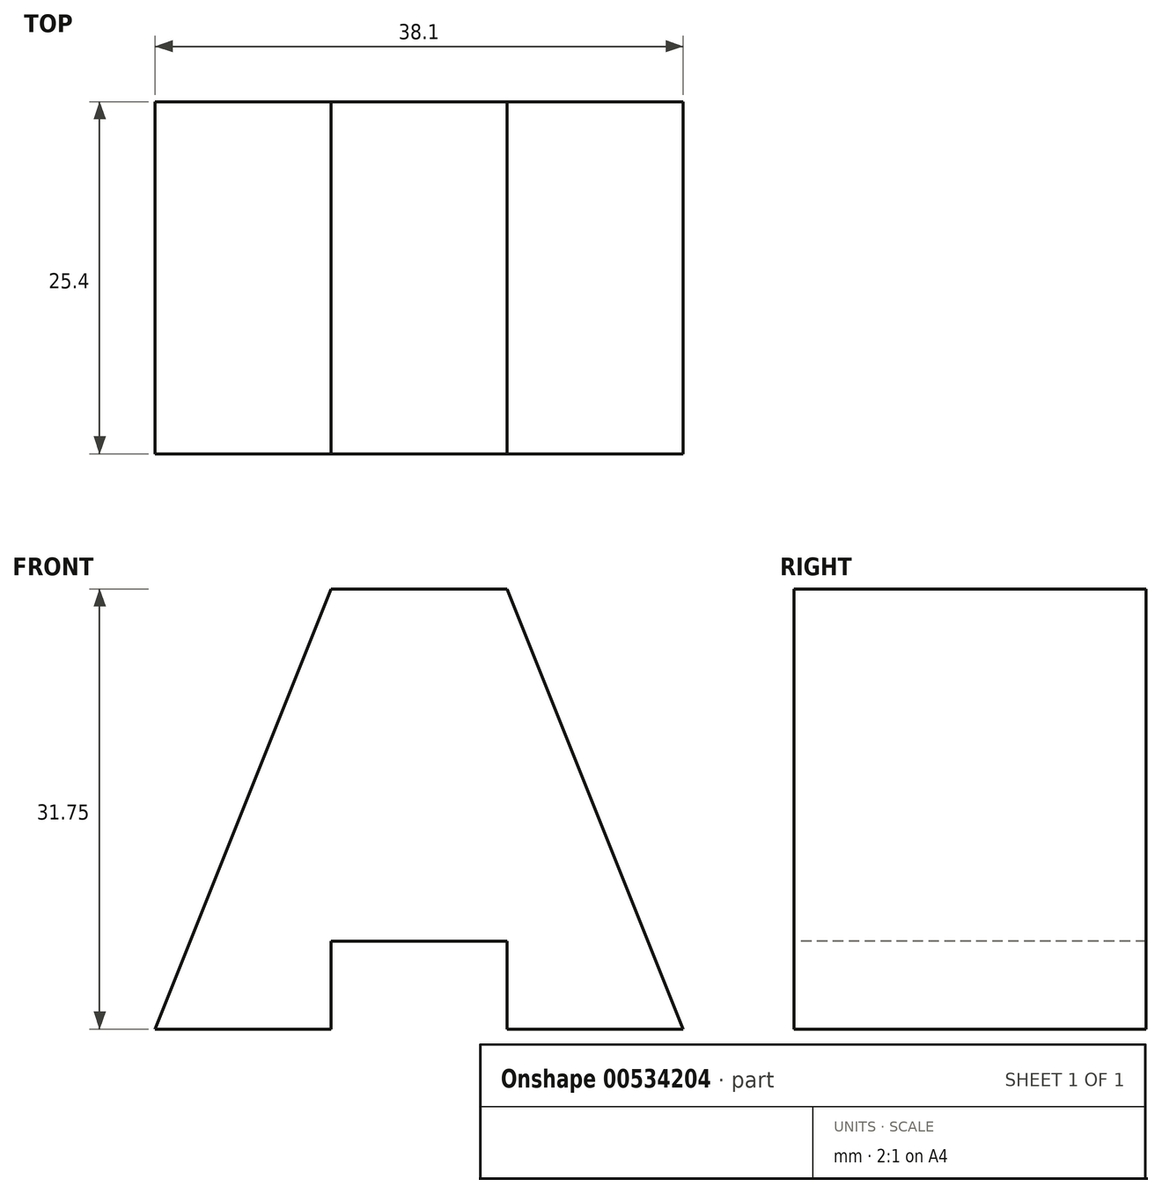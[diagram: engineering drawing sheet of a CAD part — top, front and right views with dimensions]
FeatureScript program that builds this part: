
annotation { "Feature Type Name" : "Feature", "Feature Type Description" : "" }
export const myFeature = defineFeature(function(context is Context, id is Id, definition is map)
    precondition{}
    {
        {
            var Q0;
            Q0=qCreatedBy(makeId("Front.planeOp"),FACE);
            var sketch = newSketch(context, id + "F0", { "sketchPlane" : qUnion([Q0])});
            skLineSegment(sketch, "E0", {"start": v(0, 0) * mm, "end": v(38.1, 0) * mm});
            skLineSegment(sketch, "E1", {"start": v(38.1, 0) * mm, "end": v(38.1, 31.75) * mm});
            skLineSegment(sketch, "E2", {"start": v(38.1, 31.75) * mm, "end": v(0, 31.75) * mm});
            skLineSegment(sketch, "E3", {"start": v(0, 31.75) * mm, "end": v(0, 0) * mm});
            skSolve(sketch);
        }
        {
            var Q0;
            Q0 = qSketchRegion(id + "F0", true);
            extrude(context, id + "F1", {"entities" : qUnion([Q0]), "depth" : 25.4 * mm, "offsetDistance" : 25.4 * mm});
        }
        {
            var Q0;
            Q0=makeQuery(id+"F1.opExtrude","CAP_FACE",FACE,{"disambiguationData":[OSD([sQuery(id+"F0.wireOp",EDGE,"E0"),sQuery(id+"F0.wireOp",EDGE,"E1"),sQuery(id+"F0.wireOp",EDGE,"E2"),sQuery(id+"F0.wireOp",EDGE,"E3")])],"isStart":false});
            var sketch = newSketch(context, id + "F2", { "sketchPlane" : qUnion([Q0])});
            skLineSegment(sketch, "E4", {"start": v(0, 0) * mm, "end": v(12.7, 0) * mm});
            skLineSegment(sketch, "E5", {"start": v(12.7, 0) * mm, "end": v(12.7, 6.35) * mm});
            skLineSegment(sketch, "E6", {"start": v(12.7, 6.35) * mm, "end": v(25.4, 6.35) * mm});
            skLineSegment(sketch, "E7", {"start": v(25.4, 6.35) * mm, "end": v(25.4, 0) * mm});
            skLineSegment(sketch, "E8", {"start": v(25.4, 0) * mm, "end": v(38.1, 0) * mm});
            skSolve(sketch);
        }
        {
            var Q0;
            Q0 = qSketchRegion(id + "F2", true);
            var Q1;
            {var subQ0=sQuery(id+"F2.wireOp",EDGE,"E5");Q1=makeQuery(id+"F2.imprint","IMPRINT",FACE,{"disambiguationData":[TD([[makeQuery(id+"F2.imprint","IMPRINT",EDGE,{"derivedFrom":subQ0}),-1.0]])]});}
            extrude(context, id + "F3", {"entities" : qUnion([Q0, Q1]), "operationType" : NewBodyOperationType.REMOVE, "oppositeDirection" : true, "depth" : 25.4 * mm, "offsetDistance" : 25.4 * mm});
        }
        {
            var Q0;
            Q0=makeQuery(id+"F1.opExtrude","CAP_FACE",FACE,{"disambiguationData":[OSD([sQuery(id+"F0.wireOp",EDGE,"E0"),sQuery(id+"F0.wireOp",EDGE,"E1"),sQuery(id+"F0.wireOp",EDGE,"E2"),sQuery(id+"F0.wireOp",EDGE,"E3")])],"isStart":false});
            var sketch = newSketch(context, id + "F4", { "sketchPlane" : qUnion([Q0])});
            skLineSegment(sketch, "E9", {"start": v(38.1, 0) * mm, "end": v(25.4, 31.75) * mm});
            skLineSegment(sketch, "E10", {"start": v(25.4, 31.75) * mm, "end": v(38.1, 31.75) * mm});
            skLineSegment(sketch, "E11", {"start": v(0, 0) * mm, "end": v(12.7, 31.75) * mm});
            skLineSegment(sketch, "E12", {"start": v(12.7, 31.75) * mm, "end": v(0, 31.75) * mm});
            skSolve(sketch);
        }
        {
            var Q0;
            Q0 = qSketchRegion(id + "F4", true);
            var Q1;
            Q1=makeQuery(id+"F4.imprint","IMPRINT",FACE,{"disambiguationData":[TD([[makeQuery(id+"F4.imprint","IMPRINT",EDGE,{"derivedFrom":sQuery(id+"F4.wireOp",EDGE,"E11")}),1.0]])]});
            var Q2;
            Q2=makeQuery(id+"F4.imprint","IMPRINT",FACE,{"disambiguationData":[TD([[makeQuery(id+"F4.imprint","IMPRINT",EDGE,{"derivedFrom":sQuery(id+"F4.wireOp",EDGE,"E9")}),-1.0]])]});
            extrude(context, id + "F5", {"entities" : qUnion([Q0, Q1, Q2]), "operationType" : NewBodyOperationType.REMOVE, "oppositeDirection" : true, "depth" : 25.4 * mm, "offsetDistance" : 25.4 * mm});
        }
    });
